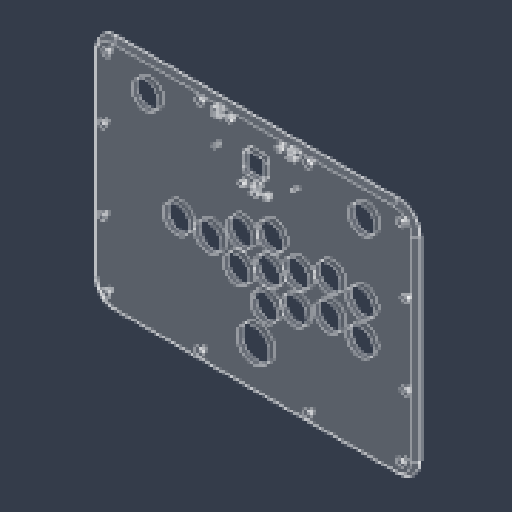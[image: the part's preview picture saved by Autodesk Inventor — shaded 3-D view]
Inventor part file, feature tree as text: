
AUTODESK INVENTOR PART (.ipt)
format: ipt  version: 2023.4 (Build 274418000, 418)  size: 305,152 bytes
history: native  units: mm
features: sketch x8, hole x5, extrude x3, mirror x2, fillet x1, chamfer x1
ambient origin geometry x8: Origin, YZ Plane, XZ Plane, XY Plane, X Axis, Y Axis, Z Axis, Center Point
bodies: Solid1 (feature_tree)
feature tree (20):
  extrude  "Extrusion1"  Depth=220.0mm
  hole  "Hole1"  [1 undecoded]
  hole  "Hole2"  [1 undecoded]
  hole  "Hole3"  [1 undecoded]
  fillet  "Fillet2"  Radius=65.3mm
  chamfer  "Chamfer1"  Distance=26.9mm
  hole  "Hole4"  [1 undecoded]
  mirror  "Mirror1"
  mirror  "Mirror2"
  extrude  "Extrusion5"  Depth=5.1mm
  hole  "Hole5"  [1 undecoded]
  extrude  "Extrusion6"  Depth=5.1mm
  sketch  "Sketch1"  dims[d0=300.0mm d1=220.0mm]
  sketch  "Sketch2"  dims[d3=0.0mm d4=40.0mm]
  sketch  "Sketch5"  dims[d5=15.5mm d6=26.3mm]
  sketch  "Sketch6"  dims[d7=29.5mm d11=52.4mm d12=65.3mm]
  sketch  "Sketch8"  dims[d13=65.2mm]
  sketch  "Sketch9"  dims[d14=9.7mm]
  sketch  "Sketch10"  dims[d15=29.4mm]
  sketch  "Sketch11"  dims[d16=2.6mm d17=26.9mm d18=29.6mm d19=29.5mm d20=1.7mm d22=46.0mm d23=30.1mm d24=96.7mm d25=91.7mm d26=31.0mm d27=31.0mm d28=35.0mm d29=25.0mm d30=6.0mm d31=3.6mm d32=2.0mm d33=90.0deg d34=8.0mm d35=20.594885mm d52=31.0mm d53=6.0mm d54=50.0mm d55=32.0mm d56=90.0deg d57=8.0mm d58=20.594885mm d61=30.0mm d62=50.0mm d63=1.482913mm d64=1.482913mm d65=40.0mm d66=40.0mm d67=71.4mm d68=38.8mm d69=3.4mm d70=6.0mm d71=4.4mm d72=2.3mm d73=90.0deg d74=8.0mm d75=20.594885mm d81=20.0mm d82=4.0mm d83=2.0mm d84=45.0deg d85=10.0mm d86=10.0mm d87=220.0mm d88=300.0mm d89=73.0mm d90=100.0mm d91=14.0mm d92=14.0mm d93=3.4mm d94=6.0mm d95=7.5mm d96=3.4mm d97=90.0deg d98=8.0mm d99=20.594885mm d100=20.0mm d101=20.0mm d102=2.0mm d103=4.0mm d104=0.0mm d105=0.0mm d106=22.5mm d107=18.0mm d108=22.5mm d109=22.5mm d110=27.4mm d111=68.8mm d112=2.9mm d113=6.0mm d114=5.5mm d115=2.9mm d116=14.3117mm d117=8.0mm d118=20.594885mm d119=8.1mm d120=5.1mm d121=2.0mm d122=8.1mm d123=5.1mm d124=2.0mm d125=8.1mm d126=5.1mm d127=2.0mm d128=0.0mm d129=0.0mm d130=11.25mm d131=11.25mm d132=11.25mm]
note: 5 required parameter values undecoded (feature->parameter linkage not recoverable at this tier; creation-order binding heuristic only, values carry confidence <= 0.55)
